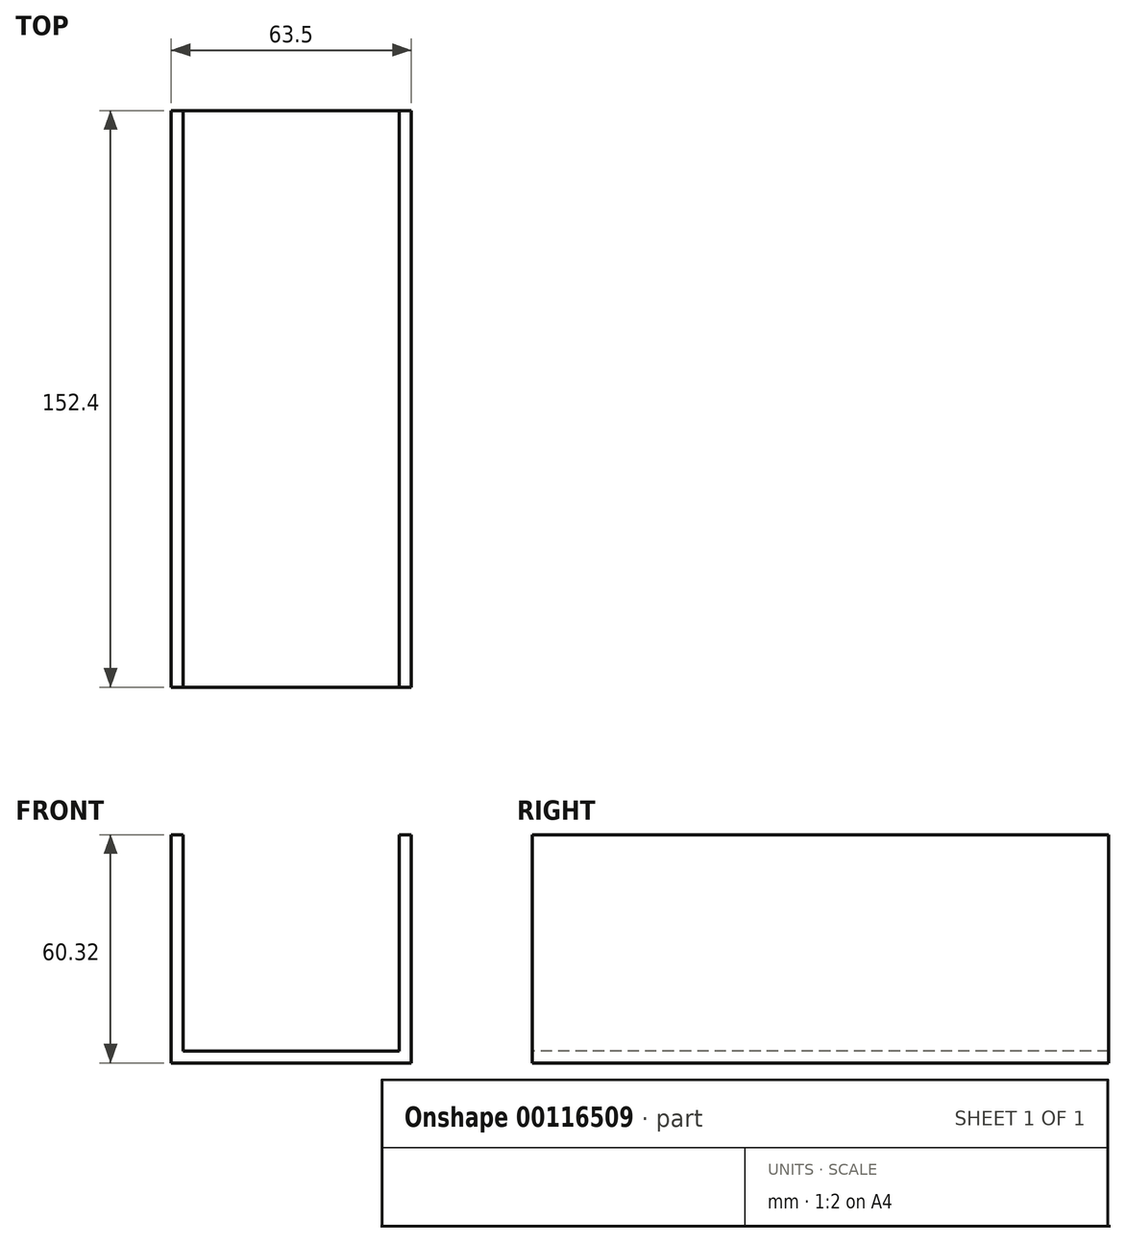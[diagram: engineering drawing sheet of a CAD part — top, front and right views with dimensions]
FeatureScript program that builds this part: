
annotation { "Feature Type Name" : "Feature", "Feature Type Description" : "" }
export const myFeature = defineFeature(function(context is Context, id is Id, definition is map)
    precondition{}
    {
        {
            var Q0;
            Q0=qCreatedBy(makeId("Front.planeOp"),FACE);
            var sketch = newSketch(context, id + "F0", { "sketchPlane" : qUnion([Q0])});
            skLineSegment(sketch, "E0.top", {"start": v(28.57, -28.57) * mm, "end": v(-28.58, -28.57) * mm});
            skLineSegment(sketch, "E0.left", {"start": v(28.58, 28.58) * mm, "end": v(28.57, -28.57) * mm});
            skLineSegment(sketch, "E0.right", {"start": v(-28.58, 28.58) * mm, "end": v(-28.58, -28.57) * mm});
            skPoint(sketch, "E0.middle", {"position": v(0, 0) * mm});
            skLineSegment(sketch, "E1.0", {"start": v(31.75, 28.58) * mm, "end": v(31.75, -31.75) * mm});
            skLineSegment(sketch, "E1.1", {"start": v(31.75, -31.75) * mm, "end": v(-31.75, -31.75) * mm});
            skLineSegment(sketch, "E1.2", {"start": v(-31.75, 28.58) * mm, "end": v(-31.75, -31.75) * mm});
            skLineSegment(sketch, "E2", {"start": v(-28.58, 28.58) * mm, "end": v(-31.75, 28.58) * mm});
            skLineSegment(sketch, "E3", {"start": v(28.58, 28.58) * mm, "end": v(31.75, 28.58) * mm});
            skSolve(sketch);
        }
        {
            var Q0;
            Q0 = qSketchRegion(id + "F0", true);
            extrude(context, id + "F1", {"entities" : qUnion([Q0]), "oppositeDirection" : true, "depth" : 152.4 * mm});
        }
    });
